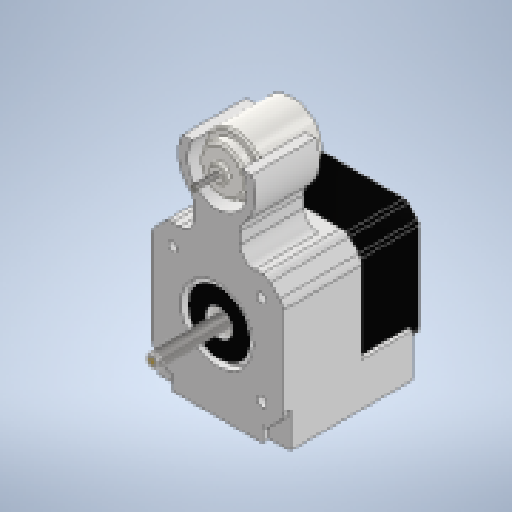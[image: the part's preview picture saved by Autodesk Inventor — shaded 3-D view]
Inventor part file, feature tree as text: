
AUTODESK INVENTOR PART (.ipt)
format: ipt  version: 2024.1 (Build 281209000, 209)  size: 681,472 bytes
history: native  units: mm
features: sketch x23, extrude x21, projected_geometry x11, fillet x10, other x5, chamfer x3
ambient origin geometry x8: Origin, YZ Plane, XZ Plane, XY Plane, X Axis, Y Axis, Z Axis, Center Point
bodies: Solid7 (feature_tree)
feature tree (73):
  other  "stepper"
  extrude  "Extrusion1"  Depth=41.8mm
  chamfer  "Chamfer1"  Distance=47.0mm
  fillet  "Fillet1"  Radius=2.0mm
  extrude  "Extrusion2"  Depth=41.8mm
  extrude  "Extrusion3"  Depth=20.9mm
  chamfer  "Chamfer2"  Distance=1.79mm
  other  "Work Point1"
  extrude  "Extrusion4"  Depth=5.0mm
  fillet  "Fillet2"  Radius=25.0mm
  extrude  "Extrusion5"  Depth=2.0mm
  extrude  "Extrusion6"  Depth=1.0mm
  extrude  "Extrusion7"  Depth=5.4mm
  extrude  "Extrusion8"  Depth=31.0mm
  extrude  "Extrusion9"  Depth=3.2mm
  extrude  "Extrusion16"  Depth=2.0mm
  fillet  "Fillet6"  Radius=2.5mm
  extrude  "Extrusion17"  Depth=42.5mm TaperAngle=0.0deg
  extrude  "Extrusion18"  Depth=5.0mm
  fillet  "Fillet7"  Radius=25.0mm
  fillet  "Fillet8"  Radius=20.9mm
  extrude  "Extrusion19"  Depth=45.8mm
  fillet  "Fillet9"  Radius=21.0mm
  extrude  "Extrusion20"  Depth=16.0mm
  fillet  "Fillet10"  Radius=3.8mm
  extrude  "Extrusion21"  Depth=6.05mm
  extrude  "Extrusion10"  Depth=2.0mm
  sketch  "Sketch11"  dims[d30=5.4mm d31=3.2mm]
  fillet  "Fillet3"  Radius=8.56mm
  extrude  "Extrusion11"  Depth=2.0mm
  fillet  "Fillet4"  Radius=18.75mm
  extrude  "Extrusion12"  Depth=5.0mm TaperAngle=45.0deg
  extrude  "Extrusion13"  Depth=33.35mm
  fillet  "Fillet5"  Radius=33.35mm
  extrude  "Extrusion14"  Depth=1.96mm
  extrude  "Extrusion15"  Depth=5.0mm
  chamfer  "Chamfer3"  Distance=6.03mm
  sketch  "Sketch17"  dims[d54=1.25mm d55=6.05mm]
  sketch  "Sketch1"  dims[d0=41.8mm d1=41.8mm d2=47.0mm d3=0.0mm]
  sketch  "Sketch2"  dims[d4=4.5mm d5=2.0mm d6=45.0deg d7=2.0mm]
  sketch  "Sketch3"  dims[d8=22.0mm d9=41.8mm]
  sketch  "Sketch4"  dims[d10=41.8mm d11=20.9mm]
  sketch  "Sketch5"  dims[d12=20.9mm d13=1.79mm d14=0.0mm]
  sketch  "Sketch6"  dims[d15=9.15mm d16=5.0mm d17=25.0mm d18=0.0mm]
  projected_geometry  "Projected Loop1"
  other  "casing"
  sketch  "Sketch7"  dims[d19=0.3mm d20=1.0mm d21=45.0deg d22=2.0mm]
  projected_geometry  "Projected Loop2"
  projected_geometry  "Projected Loop3"
  sketch  "Sketch8"  dims[d23=15.0mm d24=0.0mm d25=1.0mm]
  projected_geometry  "Projected Loop4"
  sketch  "Sketch9"  dims[d26=5.4mm d27=5.4mm]
  projected_geometry  "Projected Loop5"
  projected_geometry  "Projected Loop6"
  projected_geometry  "Projected Loop7"
  sketch  "Sketch10"  dims[d28=5.4mm d29=31.0mm]
  other  "genny"
  sketch  "Sketch12"  dims[d32=6.0mm d33=0.0mm d34=2.0mm d35=2.5mm d36=0.0mm]
  sketch  "Sketch13"  dims[d37=10.0mm d38=42.5mm d39=0.0mm]
  sketch  "Sketch14"  dims[d40=5.0mm d41=0.0mm d42=1.45mm d43=25.0mm d44=0.0mm d45=20.9mm]
  sketch  "Sketch15"  dims[d46=22.9mm d47=45.8mm d48=21.0mm d49=0.0mm]
  projected_geometry  "Projected Loop8"
  sketch  "Sketch16"  dims[d50=0.752mm d51=16.0mm d52=3.8mm d53=0.0mm]
  projected_geometry  "Projected Loop9"
  sketch  "Sketch18"  dims[d56=1.5mm d57=0.0mm d58=2.0mm d59=8.56mm d60=0.0mm]
  other  "generator"
  sketch  "Sketch19"  dims[d61=0.2mm d62=2.0mm d63=18.75mm d64=0.0mm]
  sketch  "Sketch20"  dims[d65=0.0mm d66=0.0mm d67=5.0mm d68=1.0mm d69=45.0deg]
  sketch  "Sketch21"  dims[d70=33.35mm d76=33.35mm d78=33.35mm]
  sketch  "Sketch22"  dims[d79=90.0mm d80=1.96mm]
  projected_geometry  "Projected Loop10"
  sketch  "Sketch23"  dims[d81=8.27mm d82=0.0mm d83=0.2mm d84=6.03mm d85=1.73mm d86=0.0mm d87=16.0mm d88=3.84mm d89=0.0mm d90=0.5mm d91=0.8mm d92=20.88mm d93=20.4mm d94=0.0mm d95=0.8mm d96=3.0mm d97=6.0mm d98=8.0mm d99=8.0mm d100=22.15mm d101=0.0mm d102=5.0mm d103=0.5mm d104=22.15mm d105=0.0mm]
  projected_geometry  "Projected Loop11"
